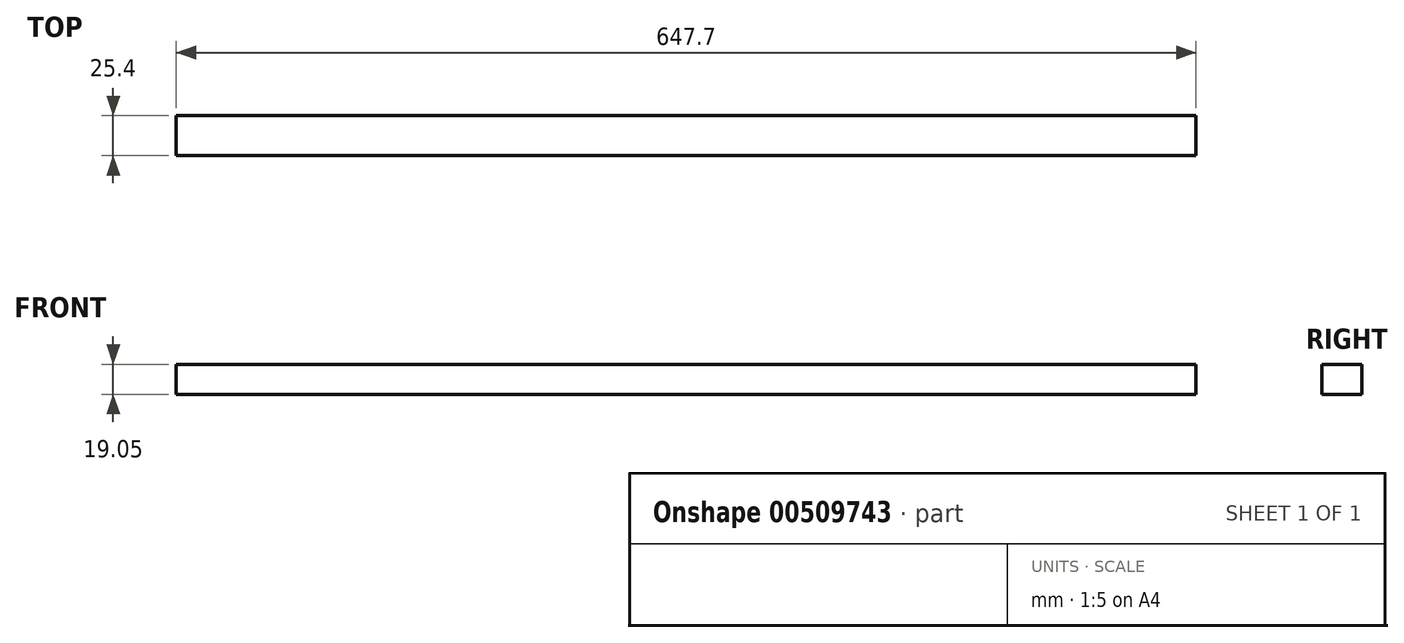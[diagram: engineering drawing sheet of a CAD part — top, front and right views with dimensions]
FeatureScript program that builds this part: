
annotation { "Feature Type Name" : "Feature", "Feature Type Description" : "" }
export const myFeature = defineFeature(function(context is Context, id is Id, definition is map)
    precondition{}
    {
        {
            var Q0;
            Q0=qCreatedBy(makeId("Front.planeOp"),FACE);
            var sketch = newSketch(context, id + "F0", { "sketchPlane" : qUnion([Q0])});
            skLineSegment(sketch, "E0.bottom", {"start": v(-283.3, 49.05) * mm, "end": v(364.4, 49.05) * mm});
            skLineSegment(sketch, "E0.top", {"start": v(-283.3, 30) * mm, "end": v(364.4, 30) * mm});
            skLineSegment(sketch, "E0.left", {"start": v(-283.3, 49.05) * mm, "end": v(-283.3, 30) * mm});
            skLineSegment(sketch, "E0.right", {"start": v(364.4, 49.05) * mm, "end": v(364.4, 30) * mm});
            skSolve(sketch);
        }
        {
            var Q0;
            Q0 = qSketchRegion(id + "F0", true);
            extrude(context, id + "F1", {"entities" : qUnion([Q0]), "depth" : 25.4 * mm});
        }
    });
